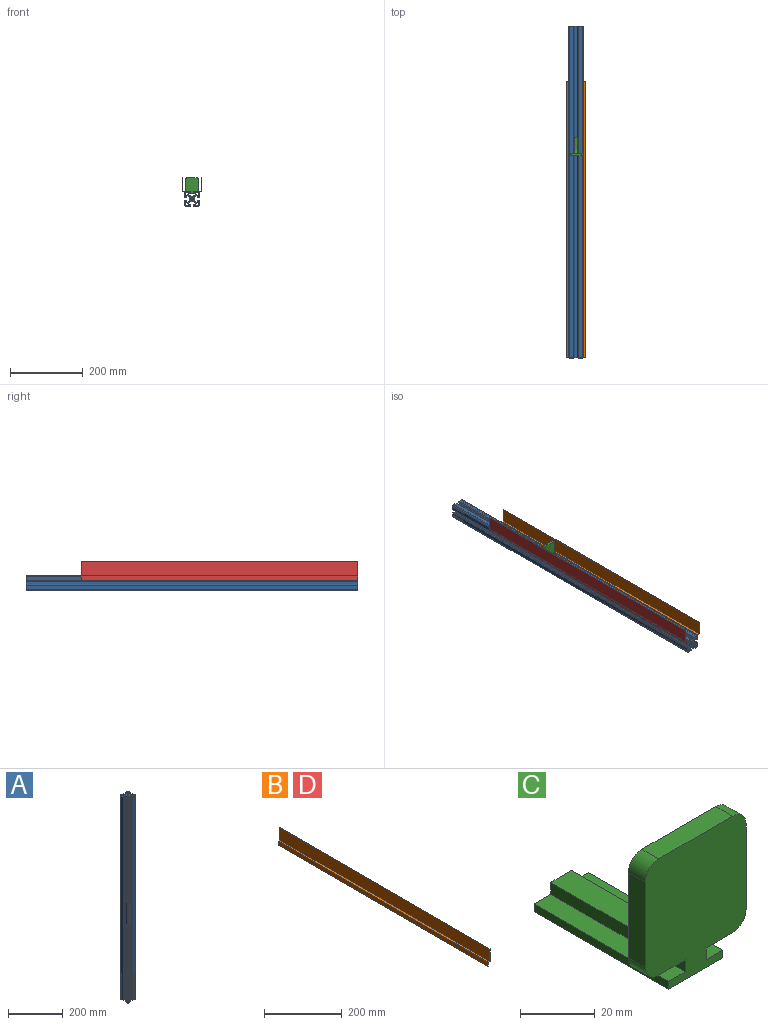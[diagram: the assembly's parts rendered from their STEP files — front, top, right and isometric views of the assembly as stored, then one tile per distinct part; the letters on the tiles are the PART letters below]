
ASSEMBLY  parts=4 mates=8
PART A: 139 faces, bbox 40x40x914.4 mm
  f0: cylinder r=4.75mm len=914.4mm, axis (0,0,-1), area 3408.6mm2, adj f1,f131,f137,f138
  f1: plane 914.4x6.72mm, normal (1,0,0), area 6141.5mm2, adj f0,f2,f137,f138
  f2: cylinder r=4.75mm len=914.4mm, axis (0,0,-1), area 3408.6mm2, adj f1,f3,f137,f138
  f3: plane 914.4x3.3mm, normal (0.71,-0.71,0), area 4269.2mm2, adj f2,f4,f137,f138
  f4: cylinder r=0.89mm len=914.4mm, axis (0,0,-1), area 639.7mm2, adj f3,f5,f137,f138
  f5: plane 914.4x2.3mm, normal (0,-1,0), area 2099.2mm2, adj f4,f6,f137,f138
  f6: cylinder r=1.27mm len=914.4mm, axis (0,0,-1), area 1824.2mm2, adj f5,f7,f137,f138
  f7: plane 914.4x2.11mm, normal (-1,0,0), area 1927.5mm2, adj f6,f8,f137,f138
  f8: plane 914.4x0.63mm, normal (0,1,0), area 575mm2, adj f7,f9,f137,f138
  f9: plane 914.4x1.14mm, normal (-1,0,0), area 1045.5mm2, adj f8,f10,f137,f138
  f10: cylinder r=1.57mm len=914.4mm, axis (0,0,-1), area 2255mm2, adj f9,f11,f137,f138
  f11: plane 914.4x0.92mm, normal (0,-1,0), area 841.2mm2, adj f10,f12,f137,f138
  f12: cylinder r=1.57mm len=914.4mm, axis (0,0,-1), area 2255mm2, adj f11,f13,f137,f138
  f13: plane 914.4x11.07mm, normal (1,0,0), area 10124.1mm2, adj f12,f14,f137,f138
  f14: cylinder r=3.17mm len=914.4mm, axis (0,0,-1), area 4553.2mm2, adj f13,f15,f137,f138
  f15: plane 914.4x11.2mm, normal (0,1,0), area 10241.3mm2, adj f14,f16,f137,f138
  f16: cylinder r=1.57mm len=914.4mm, axis (0,0,-1), area 2255.1mm2, adj f15,f17,f137,f138
  f17: plane 914.4x0.73mm, normal (-1,0,0), area 671mm2, adj f16,f18,f137,f138
  f18: cylinder r=1.57mm len=914.4mm, axis (0,0,-1), area 2255.1mm2, adj f17,f19,f137,f138
  f19: plane 914.4x1.15mm, normal (0,-1,0), area 1055.2mm2, adj f18,f20,f137,f138
  f20: plane 914.4x0.76mm, normal (1,0,0), area 695.4mm2, adj f19,f21,f137,f138
  f21: plane 914.4x2.23mm, normal (0,-1,0), area 2040.1mm2, adj f20,f22,f137,f138
  f22: cylinder r=1.27mm len=914.4mm, axis (0,0,-1), area 1824.2mm2, adj f21,f23,f137,f138
  f23: plane 914.4x2.69mm, normal (-1,0,0), area 2463.8mm2, adj f22,f24,f137,f138
  f24: cylinder r=0.89mm len=914.4mm, axis (0,0,-1), area 424.9mm2, adj f23,f25,f137,f138
  f25: plane 914.4x3.4mm, normal (-0.71,0.71,0), area 4394.1mm2, adj f24,f26,f137,f138
  f26: cylinder r=4.75mm len=914.4mm, axis (0,0,-1), area 3414mm2, adj f25,f27,f137,f138
  f27: plane 914.4x6.82mm, normal (0,1,0), area 6235.8mm2, adj f26,f28,f137,f138
  f28: cylinder r=4.75mm len=914.4mm, axis (0,0,-1), area 3414mm2, adj f27,f29,f137,f138
  f29: plane 914.4x3.4mm, normal (0.71,0.71,0), area 4394.1mm2, adj f28,f30,f137,f138
  f30: cylinder r=0.89mm len=914.4mm, axis (0,0,-1), area 424.9mm2, adj f29,f31,f137,f138
  f31: plane 914.4x2.69mm, normal (1,0,0), area 2463.8mm2, adj f30,f32,f137,f138
  f32: cylinder r=1.27mm len=914.4mm, axis (0,0,-1), area 1824.2mm2, adj f31,f33,f137,f138
  f33: plane 914.4x2.23mm, normal (0,-1,0), area 2040.1mm2, adj f32,f34,f137,f138
  f34: plane 914.4x0.76mm, normal (-1,0,0), area 695.4mm2, adj f33,f35,f137,f138
  f35: plane 914.4x1.15mm, normal (0,-1,0), area 1055.2mm2, adj f34,f36,f137,f138
  f36: cylinder r=1.57mm len=914.4mm, axis (0,0,-1), area 2255.1mm2, adj f35,f37,f137,f138
  f37: plane 914.4x0.73mm, normal (1,0,0), area 671mm2, adj f36,f38,f137,f138
  f38: cylinder r=1.57mm len=914.4mm, axis (0,0,-1), area 2255.1mm2, adj f37,f39,f137,f138
  f39: plane 914.4x11.2mm, normal (0,1,0), area 10241.3mm2, adj f38,f40,f137,f138
  f40: cylinder r=3.17mm len=914.4mm, axis (0,0,-1), area 4553.2mm2, adj f39,f41,f137,f138
  f41: plane 914.4x11.07mm, normal (-1,0,0), area 10124.1mm2, adj f40,f42,f137,f138
  f42: cylinder r=1.57mm len=914.4mm, axis (0,0,-1), area 2255mm2, adj f41,f43,f137,f138
  f43: plane 914.4x0.92mm, normal (0,-1,0), area 841.2mm2, adj f42,f44,f137,f138
  f44: cylinder r=1.57mm len=914.4mm, axis (0,0,-1), area 2255mm2, adj f43,f45,f137,f138
  f45: plane 914.4x1.14mm, normal (1,0,0), area 1045.5mm2, adj f44,f46,f137,f138
  f46: plane 914.4x0.63mm, normal (0,1,0), area 575mm2, adj f45,f47,f137,f138
  f47: plane 914.4x2.11mm, normal (1,0,0), area 1927.5mm2, adj f46,f48,f137,f138
  f48: cylinder r=1.27mm len=914.4mm, axis (0,0,-1), area 1824.2mm2, adj f47,f49,f137,f138
  f49: plane 914.4x2.3mm, normal (0,-1,0), area 2099.2mm2, adj f48,f50,f137,f138
  f50: cylinder r=0.89mm len=914.4mm, axis (0,0,-1), area 639.7mm2, adj f49,f51,f137,f138
  f51: plane 914.4x3.3mm, normal (-0.71,-0.71,0), area 4269.2mm2, adj f50,f52,f137,f138
  f52: cylinder r=4.75mm len=914.4mm, axis (0,0,-1), area 3408.6mm2, adj f51,f53,f137,f138
  f53: plane 914.4x6.72mm, normal (-1,0,0), area 6141.5mm2, adj f52,f54,f137,f138
  f54: cylinder r=4.75mm len=914.4mm, axis (0,0,-1), area 3408.6mm2, adj f53,f55,f137,f138
  f55: plane 914.4x3.3mm, normal (-0.71,0.71,0), area 4269.2mm2, adj f54,f56,f137,f138
  f56: cylinder r=0.89mm len=914.4mm, axis (0,0,-1), area 639.7mm2, adj f55,f57,f137,f138
  f57: plane 914.4x2.3mm, normal (0,1,0), area 2099.2mm2, adj f56,f58,f137,f138
  f58: cylinder r=1.27mm len=914.4mm, axis (0,0,-1), area 1824.2mm2, adj f57,f59,f137,f138
  f59: plane 914.4x2.11mm, normal (1,0,0), area 1927.5mm2, adj f58,f60,f137,f138
  f60: plane 914.4x0.63mm, normal (0,-1,0), area 575mm2, adj f59,f61,f137,f138
  f61: plane 914.4x1.14mm, normal (1,0,0), area 1045.5mm2, adj f60,f62,f137,f138
  f62: cylinder r=1.57mm len=914.4mm, axis (0,0,-1), area 2255mm2, adj f61,f63,f137,f138
  f63: plane 914.4x0.92mm, normal (0,1,0), area 841.2mm2, adj f62,f64,f137,f138
  f64: cylinder r=1.57mm len=914.4mm, axis (0,0,-1), area 2255mm2, adj f63,f65,f137,f138
  f65: plane 914.4x11.07mm, normal (-1,0,0), area 10124.1mm2, adj f64,f66,f137,f138
  f66: cylinder r=3.17mm len=914.4mm, axis (0,0,-1), area 4553.2mm2, adj f65,f67,f137,f138
  f67: plane 914.4x11.2mm, normal (0,-1,0), area 10241.3mm2, adj f66,f68,f137,f138
  f68: cylinder r=1.57mm len=914.4mm, axis (0,0,-1), area 2255.1mm2, adj f67,f69,f137,f138
  f69: plane 914.4x0.73mm, normal (1,0,0), area 671mm2, adj f68,f70,f137,f138
  f70: cylinder r=1.57mm len=914.4mm, axis (0,0,-1), area 2255.1mm2, adj f69,f71,f137,f138
  f71: plane 914.4x1.15mm, normal (0,1,0), area 1055.2mm2, adj f70,f72,f137,f138
  f72: plane 914.4x0.76mm, normal (-1,0,0), area 695.4mm2, adj f71,f73,f137,f138
  f73: plane 914.4x2.23mm, normal (0,1,0), area 2040.1mm2, adj f72,f74,f137,f138
  f74: cylinder r=1.27mm len=914.4mm, axis (0,0,-1), area 1824.2mm2, adj f73,f75,f137,f138
  f75: plane 914.4x2.69mm, normal (1,0,0), area 2463.8mm2, adj f74,f76,f137,f138
  f76: cylinder r=0.89mm len=914.4mm, axis (0,0,-1), area 424.9mm2, adj f75,f77,f137,f138
  f77: plane 914.4x3.4mm, normal (0.71,-0.71,0), area 4394.1mm2, adj f76,f78,f137,f138
  f78: cylinder r=4.75mm len=914.4mm, axis (0,0,-1), area 3414mm2, adj f77,f79,f137,f138
  f79: plane 914.4x6.82mm, normal (0,-1,0), area 6235.8mm2, adj f78,f80,f137,f138
  f80: cylinder r=4.75mm len=914.4mm, axis (0,0,-1), area 3414mm2, adj f79,f81,f137,f138
  f81: plane 914.4x3.4mm, normal (-0.71,-0.71,0), area 4394.1mm2, adj f80,f82,f137,f138
  f82: cylinder r=0.89mm len=914.4mm, axis (0,0,-1), area 424.9mm2, adj f81,f83,f137,f138
  f83: plane 914.4x2.69mm, normal (-1,0,0), area 2463.8mm2, adj f82,f84,f137,f138
  f84: cylinder r=1.27mm len=914.4mm, axis (0,0,-1), area 1824.2mm2, adj f83,f85,f137,f138
  f85: plane 914.4x2.23mm, normal (0,1,0), area 2040.1mm2, adj f84,f86,f137,f138
  f86: plane 914.4x0.76mm, normal (1,0,0), area 695.4mm2, adj f85,f87,f137,f138
  f87: plane 914.4x1.15mm, normal (0,1,0), area 1055.2mm2, adj f86,f88,f137,f138
  f88: cylinder r=1.57mm len=914.4mm, axis (0,0,-1), area 2255.1mm2, adj f87,f89,f137,f138
  f89: plane 914.4x0.73mm, normal (-1,0,0), area 671mm2, adj f88,f90,f137,f138
  f90: cylinder r=1.57mm len=914.4mm, axis (0,0,-1), area 2255.1mm2, adj f89,f91,f137,f138
  f91: plane 914.4x11.2mm, normal (0,-1,0), area 10241.3mm2, adj f90,f92,f137,f138
  f92: cylinder r=3.17mm len=914.4mm, axis (0,0,-1), area 4553.2mm2, adj f91,f93,f137,f138
  f93: plane 914.4x11.07mm, normal (1,0,0), area 10124.1mm2, adj f92,f94,f137,f138
  f94: cylinder r=1.57mm len=914.4mm, axis (0,0,-1), area 2255mm2, adj f93,f95,f137,f138
  f95: plane 914.4x0.92mm, normal (0,1,0), area 841.2mm2, adj f94,f96,f137,f138
  f96: cylinder r=1.57mm len=914.4mm, axis (0,0,-1), area 2255mm2, adj f95,f97,f137,f138
  f97: plane 914.4x1.14mm, normal (-1,0,0), area 1045.5mm2, adj f96,f98,f137,f138
  f98: plane 914.4x0.63mm, normal (0,-1,0), area 575mm2, adj f97,f99,f137,f138
  f99: plane 914.4x2.11mm, normal (-1,0,0), area 1927.5mm2, adj f98,f100,f137,f138
  f100: cylinder r=1.27mm len=914.4mm, axis (0,0,-1), area 1824.2mm2, adj f99,f101,f137,f138
  f101: plane 914.4x2.3mm, normal (0,1,0), area 2099.2mm2, adj f100,f102,f137,f138
  f102: cylinder r=0.89mm len=914.4mm, axis (0,0,-1), area 639.7mm2, adj f101,f131,f137,f138
  f103: cylinder r=2.8mm len=914.4mm, axis (0,0,-1), area 4021.7mm2, adj f104,f132,f137,f138
  f104: plane 914.4x2.98mm, normal (-1,0,0), area 2724.9mm2, adj f103,f105,f137,f138
  f105: cylinder r=0.63mm len=914.4mm, axis (0,0,-1), area 904.9mm2, adj f104,f106,f137,f138
  f106: plane 914.4x4.51mm, normal (0,1,0), area 4123.9mm2, adj f105,f107,f137,f138
  f107: cylinder r=1.27mm len=914.4mm, axis (0,0,-1), area 1824.2mm2, adj f106,f108,f137,f138
  f108: plane 914.4x4.51mm, normal (1,0,0), area 4123.9mm2, adj f107,f109,f137,f138
  f109: cylinder r=0.63mm len=914.4mm, axis (0,0,-1), area 904.9mm2, adj f108,f132,f137,f138
  f110: cylinder r=2.8mm len=914.4mm, axis (0,0,-1), area 4021.7mm2, adj f111,f133,f137,f138
  f111: plane 914.4x2.98mm, normal (1,0,0), area 2724.9mm2, adj f110,f112,f137,f138
  f112: cylinder r=0.63mm len=914.4mm, axis (0,0,-1), area 904.9mm2, adj f111,f113,f137,f138
  f113: plane 914.4x4.51mm, normal (0,-1,0), area 4123.9mm2, adj f112,f114,f137,f138
  f114: cylinder r=1.27mm len=914.4mm, axis (0,0,-1), area 1824.2mm2, adj f113,f115,f137,f138
  f115: plane 914.4x4.51mm, normal (-1,0,0), area 4123.9mm2, adj f114,f116,f137,f138
  f116: cylinder r=0.63mm len=914.4mm, axis (0,0,-1), area 904.9mm2, adj f115,f133,f137,f138
  f117: cylinder r=0.63mm len=914.4mm, axis (0,0,-1), area 904.9mm2, adj f118,f134,f137,f138
  f118: plane 914.4x2.98mm, normal (-1,0,0), area 2724.9mm2, adj f117,f119,f137,f138
  f119: cylinder r=2.8mm len=914.4mm, axis (0,0,-1), area 4021.7mm2, adj f118,f120,f137,f138
  f120: plane 914.4x2.98mm, normal (0,1,0), area 2724.9mm2, adj f119,f121,f137,f138
  f121: cylinder r=0.63mm len=914.4mm, axis (0,0,-1), area 904.9mm2, adj f120,f122,f137,f138
  f122: plane 914.4x4.51mm, normal (1,0,0), area 4123.9mm2, adj f121,f123,f137,f138
  f123: cylinder r=1.27mm len=914.4mm, axis (0,0,-1), area 1824.2mm2, adj f122,f134,f137,f138
  f124: cylinder r=2.8mm len=914.4mm, axis (0,0,-1), area 4021.7mm2, adj f125,f135,f137,f138
  f125: plane 914.4x2.98mm, normal (0,-1,0), area 2724.9mm2, adj f124,f126,f137,f138
  f126: cylinder r=0.63mm len=914.4mm, axis (0,0,-1), area 904.9mm2, adj f125,f127,f137,f138
  f127: plane 914.4x4.51mm, normal (-1,0,0), area 4123.9mm2, adj f126,f128,f137,f138
  f128: cylinder r=1.27mm len=914.4mm, axis (0,0,-1), area 1824.2mm2, adj f127,f129,f137,f138
  f129: plane 914.4x4.51mm, normal (0,1,0), area 4123.9mm2, adj f128,f130,f137,f138
  f130: cylinder r=0.63mm len=914.4mm, axis (0,0,-1), area 904.9mm2, adj f129,f135,f137,f138
  f131: plane 914.4x3.3mm, normal (0.71,0.71,0), area 4269.2mm2, adj f0,f102,f137,f138
  f132: plane 914.4x2.98mm, normal (0,-1,0), area 2724.9mm2, adj f103,f109,f137,f138
  f133: plane 914.4x2.98mm, normal (0,1,0), area 2724.9mm2, adj f110,f116,f137,f138
  f134: plane 914.4x4.51mm, normal (0,-1,0), area 4123.9mm2, adj f117,f123,f137,f138
  f135: plane 914.4x2.98mm, normal (1,0,0), area 2724.9mm2, adj f124,f130,f137,f138
  f136: cylinder r=3.4mm len=914.4mm, axis (0,0,-1), area 19534.2mm2, adj f137,f138
  f137: plane 40x40mm, normal (0,0,1), area 658.3mm2, adj f0,f1,f2,f3,f4,f5,f6,f7
  f138: plane 40x40mm, normal (0,0,-1), area 658.3mm2, adj f0,f1,f2,f3,f4,f5,f6,f7
PART B: 10 faces, bbox 7.4x762x50.8 mm
  f0: plane 762x12.7mm, normal (-1,0,0), area 9677.4mm2, adj f1,f7,f8,f9
  f1: plane 762x0.76mm, normal (0,0,-1), area 580.6mm2, adj f0,f2,f8,f9
  f2: plane 762x11.94mm, normal (1,0,0), area 9096.8mm2, adj f1,f3,f8,f9
  f3: plane 762x6.67mm, normal (0,0,-1), area 5080.6mm2, adj f2,f4,f8,f9
  f4: plane 762x38.86mm, normal (1,0,0), area 29612.8mm2, adj f3,f5,f8,f9
  f5: plane 762x0.76mm, normal (0,0,1), area 580.6mm2, adj f4,f6,f8,f9
  f6: plane 762x38.1mm, normal (-1,0,0), area 29032.2mm2, adj f5,f7,f8,f9
  f7: plane 762x6.67mm, normal (0,0,1), area 5080.6mm2, adj f0,f6,f8,f9
  f8: plane 50.8x7.43mm, normal (0,-1,0), area 43.8mm2, adj f0,f1,f2,f3,f4,f5,f6,f7
  f9: plane 50.8x7.43mm, normal (0,1,0), area 43.8mm2, adj f0,f1,f2,f3,f4,f5,f6,f7
PART C: 21 faces, bbox 38.1x50.8x44.5 mm
  f0: plane 34.93x7.87mm, normal (0,0,1), area 275mm2, adj f5,f6,f10,f16
  f1: plane 38.1x38.1mm, normal (0,1,0), area 1354.5mm2, adj f5,f6,f11,f12,f13,f14,f15,f16
  f2: plane 50.8x20.57mm, normal (0,0,-1), area 1045.2mm2, adj f3,f8,f9,f10
  f3: plane 50.8x2.54mm, normal (1,0,0), area 129mm2, adj f2,f4,f9,f10
  f4: plane 50.8x6.35mm, normal (0,0,1), area 322.6mm2, adj f3,f5,f9,f10
  f5: plane 50.8x13.41mm, normal (1,0,0), area 242.8mm2, adj f0,f1,f4,f9,f10,f11,f16
  f6: plane 50.8x13.41mm, normal (-1,0,0), area 242.8mm2, adj f0,f1,f7,f9,f10,f12,f16
  f7: plane 50.8x6.35mm, normal (0,0,1), area 322.6mm2, adj f6,f8,f9,f10
  f8: plane 50.8x2.54mm, normal (-1,0,0), area 129mm2, adj f2,f7,f9,f10
  f9: plane 44.53x38.1mm, normal (0,-1,0), area 1512.3mm2, adj f2,f3,f4,f5,f6,f7,f8,f11
  f10: plane 20.57x6.43mm, normal (0,1,0), area 82.9mm2, adj f0,f2,f3,f4,f5,f6,f7,f8
  f11: plane 10.03x6.35mm, normal (0,0,-1), area 63.7mm2, adj f1,f5,f9,f17
  f12: plane 10.03x6.35mm, normal (0,0,-1), area 63.7mm2, adj f1,f6,f9,f20
  f13: plane 27.94x6.35mm, normal (1,0,0), area 177.4mm2, adj f1,f9,f17,f18
  f14: plane 27.94x6.35mm, normal (0,0,1), area 177.4mm2, adj f1,f9,f18,f19
  f15: plane 27.94x6.35mm, normal (-1,0,0), area 177.4mm2, adj f1,f9,f19,f20
  f16: plane 9.53x9.53mm, normal (0,0.71,0.71), area 106.1mm2, adj f0,f1,f5,f6
  f17: cylinder r=5.08mm len=6.35mm, axis (0,1,0), area 50.7mm2, adj f1,f9,f11,f13
  f18: cylinder r=5.08mm len=6.35mm, axis (0,-1,0), area 50.7mm2, adj f1,f9,f13,f14
  f19: cylinder r=5.08mm len=6.35mm, axis (0,1,0), area 50.7mm2, adj f1,f9,f14,f15
  f20: cylinder r=5.08mm len=6.35mm, axis (0,-1,0), area 50.7mm2, adj f1,f9,f12,f15
PART D: same geometry as B
PLACE A rot(axis=(-1,0,0),90deg) t=(0,-0.85,0.36)mm fixed
PLACE B t=(20,761.15,7.66)mm
PLACE C t=(-0.12,606.41,13.93)mm
PLACE D rot(axis=(0,0,1),180deg) t=(-20,-0.85,7.66)mm
MATE planar D.f9 <-> A.f138  axis (0,-1,0) through (-20.76,-0.85,19.6)mm
MATE planar D.f0 <-> A.f65  axis (1,0,0) through (-20,380.15,14.01)mm
MATE planar B.f0 <-> A.f93  axis (-1,0,0) through (20,380.15,20.36)mm
MATE planar A.f138 <-> B.f8  axis (0,-1,0) through (10.73,-0.85,8.72)mm
MATE planar C.f0 <-> A.f67  axis (0,0,1) through (-0.12,588.95,20.36)mm
MATE planar C.f6 <-> A.f69  axis (-1,0,0) through (-4.06,578.04,19.37)mm
MATE planar B.f7 <-> A.f91  axis (0,0,1) through (23.34,-0.85,20.36)mm
MATE planar D.f7 <-> A.f67  axis (0,0,1) through (-23.33,761.15,20.36)mm
